# Revit family: Shower_Arm-GROHE-Rainshower-27217_Series
name_source: partatom
category: Plumbing Fixtures
revit_build: Autodesk Revit 2014 (Build: 20130308_1515(x64)
units: mm (PartAtom-declared; Revit-internal decimal feet)

## types (2) — shared parameters
Assembly Code = D2010710
CW Connection = Yes
CWFU = 3
CalGreen Compliant = Yes
Cold Water Connection Diameter = 1/2"
Cold Water Connection Radius = 1/4"
Default Elevation = 0"
Description = Rainshower®
Flow Rate = 2.0 gpm (7.6 L/min)
HW Connection = Yes
HWFU = 3
Height = 5 3/4"
Hot Water Connection Diameter = 1"
Hot Water Connection Radius = 1/4"
Installation Type = Ceiling-Mount
Manufacturer = Grohe
Price = Prices may vary. Please consult Manufacturer Representative for most up-to-date price list.
Product Page URL = https://www.grohe.us
Tempered Connection Diameter = 1/2"
Tempered Connection Radius = 1/4"
URL = https://www.grohe.us
Vent Connection = No
WFU = 4
Warranty Documentation Link = https://cdn.cloud.grohe.com
Waste Connection = No
cUPC Compliant = Yes

## per-type parameters (varying)
| type | Finish | Material |
| 27217000 | Metal-Grohe-000-Chrome | Metal-Grohe-000-Chrome |
| 27217EN0 | Metal-Grohe-EN0-Brushed Nickel | Metal-Grohe-EN0-Brushed Nickel |

note: column(s) folded — value = type name in every type: Model

## geometry (parser evidence)
native form markers: Sweep x3
no freeform markers — native parametric forms only
